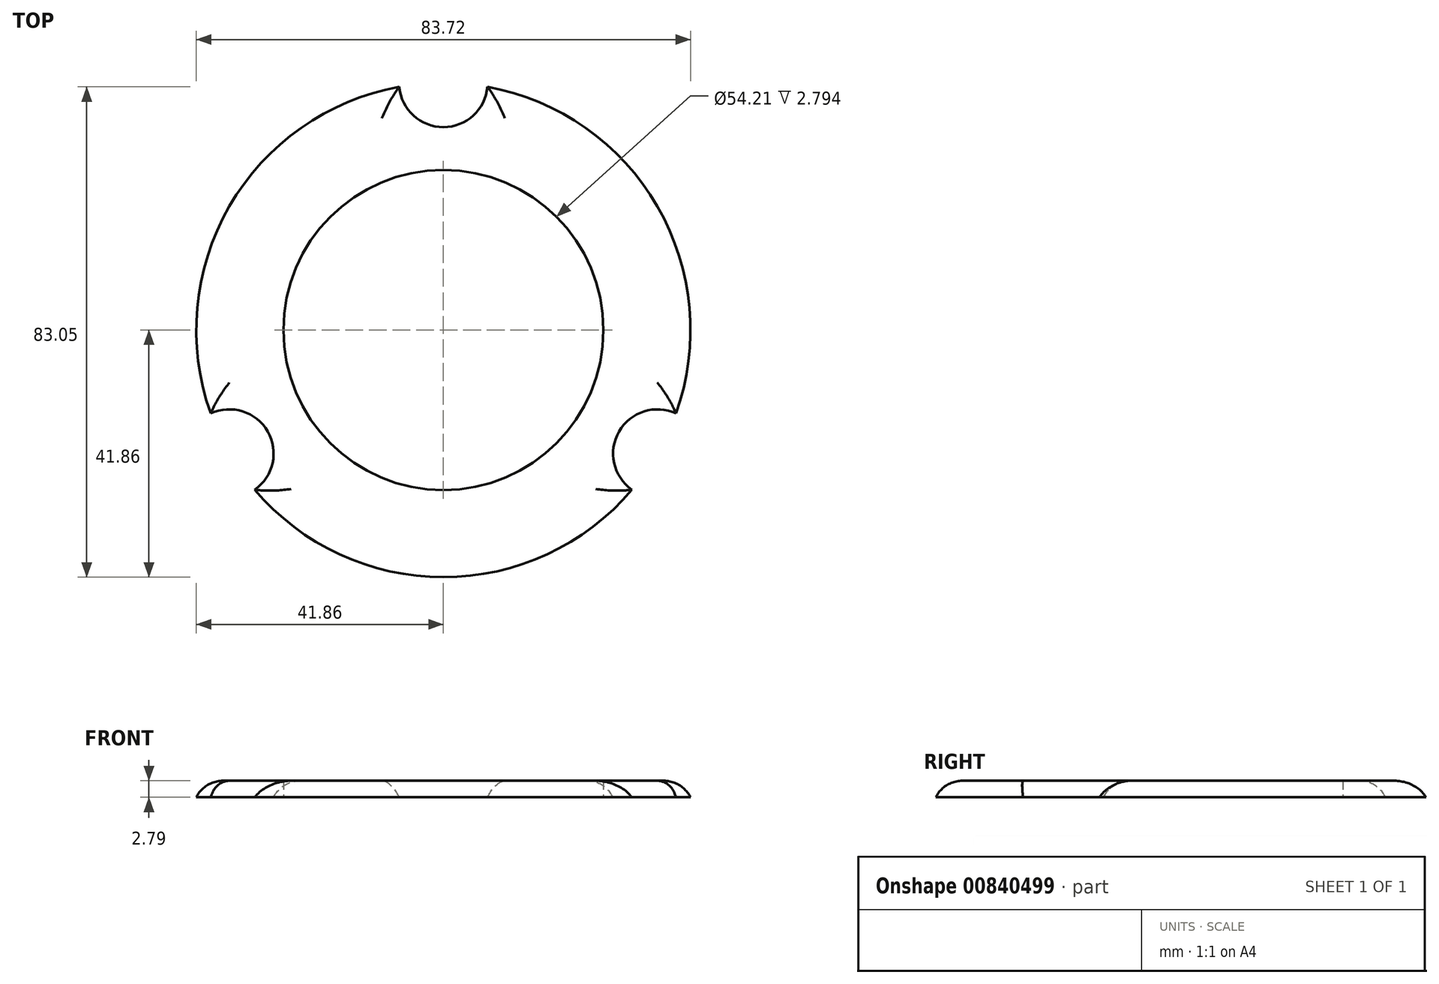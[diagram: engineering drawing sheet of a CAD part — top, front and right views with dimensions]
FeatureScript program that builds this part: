
annotation { "Feature Type Name" : "Feature", "Feature Type Description" : "" }
export const myFeature = defineFeature(function(context is Context, id is Id, definition is map)
    precondition{}
    {
        {
            var Q0;
            Q0=qCreatedBy(makeId("Top.planeOp"),FACE);
            var sketch = newSketch(context, id + "F0", { "sketchPlane" : qUnion([Q0])});
            skCircle(sketch, "E0", {"center": v(0, 0) * mm, "radius": 41.86 * mm});
            skCircle(sketch, "E1", {"center": v(0, 41.86) * mm, "radius": 7.5 * mm});
            skCircle(sketch, "E2.1.0", {"center": v(36.25, -20.93) * mm, "radius": 7.5 * mm});
            skCircle(sketch, "E2.2.0", {"center": v(-36.25, -20.93) * mm, "radius": 7.5 * mm});
            skLineSegment(sketch, "E2.anchor1", {"start": v(0, 0) * mm, "end": v(0, 41.86) * mm, "construction": true});
            skLineSegment(sketch, "E2.anchor2", {"start": v(0, 0) * mm, "end": v(-36.25, -20.93) * mm, "construction": true});
            skCircle(sketch, "E3", {"center": v(0, 0) * mm, "radius": 27.1 * mm});
            skSolve(sketch);
        }
        {
            var Q0;
            Q0=makeQuery(id+"F0.imprint","IMPRINT",FACE,{"disambiguationData":[TD([[makeQuery(id+"F0.imprint","IMPRINT",EDGE,{"derivedFrom":sQuery(id+"F0.wireOp",EDGE,"E3")}),-1.0]])]});
            extrude(context, id + "F1", {"entities" : qUnion([Q0]), "depth" : 2.8 * mm, "offsetDistance" : 25.4 * mm});
        }
        {
            var Q0;
            {var subQ0=sQuery(id+"F0.wireOp",EDGE,"E0");Q0=makeQuery(id+"F1.opExtrude","CAP_EDGE",EDGE,{"disambiguationData":[OSD([subQ0]),TDD([makeQuery(id+"F0.imprint","IMPRINT",EDGE,{"disambiguationData":[TD([[makeQuery(id+"F0.imprint","INTERSECT",VERTEX,{"disambiguationData":[OD(1.0)],"derivedFrom":[subQ0,sQuery(id+"F0.wireOp",EDGE,"E1")]}),1.0]])],"derivedFrom":subQ0})])],"isStart":false});}
            var Q1;
            Q1=makeQuery(id+"F1.opExtrude","CAP_EDGE",EDGE,{"disambiguationData":[OSD([sQuery(id+"F0.wireOp",EDGE,"E2.1.0")])],"isStart":false});
            var Q2;
            {var subQ0=sQuery(id+"F0.wireOp",EDGE,"E0");Q2=makeQuery(id+"F1.opExtrude","CAP_EDGE",EDGE,{"disambiguationData":[OSD([subQ0]),TDD([makeQuery(id+"F0.imprint","IMPRINT",EDGE,{"disambiguationData":[TD([[makeQuery(id+"F0.imprint","INTERSECT",VERTEX,{"disambiguationData":[OD(1.0)],"derivedFrom":[subQ0,sQuery(id+"F0.wireOp",EDGE,"E2.2.0")]}),-1.0]])],"derivedFrom":subQ0})])],"isStart":false});}
            var Q3;
            Q3=makeQuery(id+"F1.opExtrude","CAP_EDGE",EDGE,{"disambiguationData":[OSD([sQuery(id+"F0.wireOp",EDGE,"E2.2.0")])],"isStart":false});
            var Q4;
            {var subQ0=sQuery(id+"F0.wireOp",EDGE,"E0");Q4=makeQuery(id+"F1.opExtrude","CAP_EDGE",EDGE,{"disambiguationData":[OSD([subQ0]),TDD([makeQuery(id+"F0.imprint","IMPRINT",EDGE,{"disambiguationData":[TD([[makeQuery(id+"F0.imprint","INTERSECT",VERTEX,{"disambiguationData":[OD(0.0)],"derivedFrom":[subQ0,sQuery(id+"F0.wireOp",EDGE,"E1")]}),-1.0]])],"derivedFrom":subQ0})])],"isStart":false});}
            var Q5;
            Q5=makeQuery(id+"F1.opExtrude","CAP_EDGE",EDGE,{"disambiguationData":[OSD([sQuery(id+"F0.wireOp",EDGE,"E1")])],"isStart":false});
            fillet(context, id + "F2", {"entities" : qUnion([Q0, Q1, Q2, Q3, Q4, Q5]), "radius" : 5.08 * mm, "tangentPropagation" : true, "allowEdgeOverflow" : false});
        }
    });
